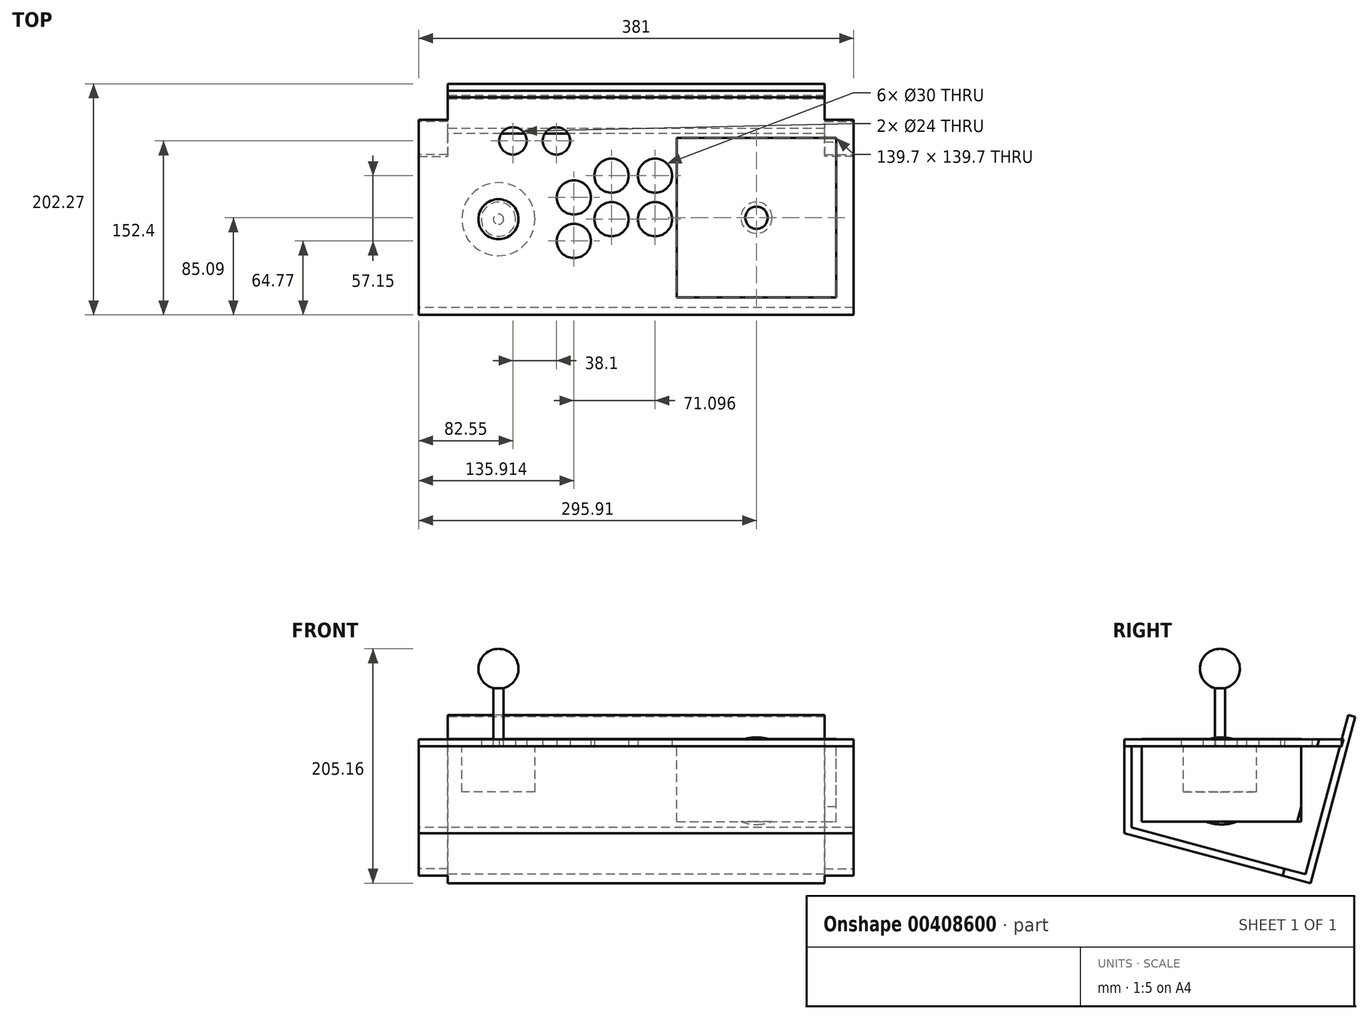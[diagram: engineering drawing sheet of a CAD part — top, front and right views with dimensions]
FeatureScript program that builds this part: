
annotation { "Feature Type Name" : "Feature", "Feature Type Description" : "" }
export const myFeature = defineFeature(function(context is Context, id is Id, definition is map)
    precondition{}
    {
        {
            assignVariable(context, id + "F0", {"variableType" : VariableType.LENGTH, "name" : "EndWidth", "lengthValue" : 381 * mm});
        }
        {
            assignVariable(context, id + "F1", {"variableType" : VariableType.LENGTH, "name" : "StickInset", "lengthValue" : 69.85 * mm});
        }
        {
            var Q0;
            Q0=qCreatedBy(makeId("Top.planeOp"),FACE);
            var sketch = newSketch(context, id + "F2", { "sketchPlane" : qUnion([Q0])});
            skLineSegment(sketch, "E0", {"start": v(0, 0) * mm, "end": v(381, 0) * mm});
            skLineSegment(sketch, "E1", {"start": v(381, 0) * mm, "end": v(381, 171.45) * mm});
            skLineSegment(sketch, "E2", {"start": v(381, 171.45) * mm, "end": v(361.95, 171.45) * mm});
            skLineSegment(sketch, "E3", {"start": v(361.95, 171.45) * mm, "end": v(361.95, 190.5) * mm});
            skLineSegment(sketch, "E4", {"start": v(0, 0) * mm, "end": v(0, 171.45) * mm});
            skLineSegment(sketch, "E5", {"start": v(0, 171.45) * mm, "end": v(19.05, 171.45) * mm});
            skLineSegment(sketch, "E6", {"start": v(19.05, 171.45) * mm, "end": v(19.05, 190.5) * mm});
            skCircle(sketch, "E7", {"center": v(82.55, 152.4) * mm, "radius": 12 * mm});
            skCircle(sketch, "E8", {"center": v(120.65, 152.4) * mm, "radius": 12 * mm});
            skCircle(sketch, "E9", {"center": v(135.91, 102.87) * mm, "radius": 15 * mm});
            skCircle(sketch, "E10", {"center": v(168.91, 121.92) * mm, "radius": 15 * mm});
            skCircle(sketch, "E11", {"center": v(207.01, 121.92) * mm, "radius": 15 * mm});
            skLineSegment(sketch, "E12", {"start": v(135.91, 102.87) * mm, "end": v(168.91, 121.92) * mm, "construction": true});
            skLineSegment(sketch, "E13", {"start": v(207.01, 121.92) * mm, "end": v(168.91, 121.92) * mm, "construction": true});
            skCircle(sketch, "E14", {"center": v(135.91, 64.77) * mm, "radius": 15 * mm});
            skCircle(sketch, "E15", {"center": v(168.91, 83.82) * mm, "radius": 15 * mm});
            skCircle(sketch, "E16", {"center": v(207.01, 83.82) * mm, "radius": 15 * mm});
            skLineSegment(sketch, "E17", {"start": v(135.91, 64.77) * mm, "end": v(168.91, 83.82) * mm, "construction": true});
            skLineSegment(sketch, "E18", {"start": v(207.01, 83.82) * mm, "end": v(168.91, 83.82) * mm, "construction": true});
            skLineSegment(sketch, "E19", {"start": v(168.91, 121.92) * mm, "end": v(168.91, 83.82) * mm, "construction": true});
            skLineSegment(sketch, "E20", {"start": v(82.55, 152.4) * mm, "end": v(120.65, 152.4) * mm, "construction": true});
            skPoint(sketch, "E21", {"position": v(168.91, 102.87) * mm});
            skLineSegment(sketch, "E22", {"start": v(135.91, 64.77) * mm, "end": v(135.91, 102.87) * mm, "construction": true});
            skCircle(sketch, "E23", {"center": v(69.85, 83.82) * mm, "radius": 15 * mm});
            skLineSegment(sketch, "E24.bottom", {"start": v(226.06, 154.94) * mm, "end": v(365.76, 154.94) * mm});
            skLineSegment(sketch, "E24.top", {"start": v(226.06, 15.24) * mm, "end": v(365.76, 15.24) * mm});
            skLineSegment(sketch, "E24.left", {"start": v(226.06, 154.94) * mm, "end": v(226.06, 15.24) * mm});
            skLineSegment(sketch, "E24.right", {"start": v(365.76, 154.94) * mm, "end": v(365.76, 15.24) * mm});
            skLineSegment(sketch, "E25", {"start": v(19.05, 190.5) * mm, "end": v(361.95, 190.5) * mm});
            skSolve(sketch);
        }
        {
            var Q0;
            Q0=makeQuery(id+"F2.imprint","IMPRINT",FACE,{"disambiguationData":[TD([[makeQuery(id+"F2.imprint","IMPRINT",EDGE,{"derivedFrom":sQuery(id+"F2.wireOp",EDGE,"E0")}),1.0]])]});
            extrude(context, id + "F3", {"entities" : qUnion([Q0]), "depth" : 6 * mm, "offsetDistance" : 25.4 * mm});
        }
        {
            var Q0;
            Q0=makeQuery(id+"F3.opExtrude","CAP_EDGE",EDGE,{"disambiguationData":[OSD([sQuery(id+"F2.wireOp",EDGE,"E24.bottom")])],"isStart":true});
            cPoint(context, id + "F4", {"entities" : qUnion([Q0]), "parameter" : 0.5});
        }
        {
            var Q0;
            Q0=makeQuery(id+"F3.opExtrude","CAP_EDGE",EDGE,{"disambiguationData":[OSD([sQuery(id+"F2.wireOp",EDGE,"E24.bottom")])],"isStart":false});
            cPoint(context, id + "F5", {"entities" : qUnion([Q0]), "parameter" : 0.5});
        }
        {
            var Q0;
            Q0=makeQuery(id+"F3.opExtrude","CAP_EDGE",EDGE,{"disambiguationData":[OSD([sQuery(id+"F2.wireOp",EDGE,"E24.top")])],"isStart":false});
            cPoint(context, id + "F6", {"entities" : qUnion([Q0]), "parameter" : 0.5});
        }
        {
            var Q0;
            Q0 = qCreatedBy(id + "F4" ,VERTEX);
            var Q1;
            Q1 = qCreatedBy(id + "F5" ,VERTEX);
            var Q2;
            Q2 = qCreatedBy(id + "F6" ,VERTEX);
            cPlane(context, id + "F7", {"entities" : qUnion([Q0, Q1, Q2]), "cplaneType" : CPlaneType.THREE_POINT, "offset" : 25.4 * mm, "width" : 152.4 * mm, "height" : 152.4 * mm});
        }
        {
            var Q0;
            Q0=qCreatedBy(makeId("Right.planeOp"),FACE);
            cPlane(context, id + "F8", {"entities" : qUnion([Q0]), "cplaneType" : CPlaneType.OFFSET, "offset" : getVariable(context, 'StickInset'), "width" : 152.4 * mm, "height" : 152.4 * mm});
        }
        {
            var Q0;
            Q0=qCreatedBy(id+"F8.planeOp",FACE);
            var sketch = newSketch(context, id + "F9", { "sketchPlane" : qUnion([Q0])});
            skArc(sketch, "E26", {"start": v(83.82, 85.21) * mm, "mid": v(66.47, 69.98) * mm, "end": v(79.32, 50.8) * mm});
            skLineSegment(sketch, "E27", {"start": v(83.82, 85.21) * mm, "end": v(83.82, -40) * mm});
            skLineSegment(sketch, "E28.0", {"start": v(79.32, 50.8) * mm, "end": v(79.32, 0) * mm});
            skLineSegment(sketch, "E29", {"start": v(83.82, -40) * mm, "end": v(51.82, -40) * mm});
            skLineSegment(sketch, "E30", {"start": v(51.82, -40) * mm, "end": v(51.82, 0) * mm});
            skLineSegment(sketch, "E31", {"start": v(51.82, 0) * mm, "end": v(79.32, 0) * mm});
            skPoint(sketch, "E32.orphan", {"position": v(83.82, 102.1) * mm});
            skSolve(sketch);
        }
        {
            var Q0;
            Q0 = qSketchRegion(id + "F9", true);
            var Q1;
            Q1=sQuery(id+"F9.wireOp",EDGE,"E27");
            revolve(context, id + "F10", {"operationType" : NewBodyOperationType.ADD, "surfaceOperationType" : NewSurfaceOperationType.NEW, "entities" : qUnion([Q0]), "axis" : qUnion([Q1]), "revolveType" : RevolveType.FULL});
        }
        {
            var Q0;
            Q0=qCreatedBy(id+"F7.planeOp",FACE);
            var sketch = newSketch(context, id + "F11", { "sketchPlane" : qUnion([Q0])});
            skArc(sketch, "E33", {"start": v(-85.1, -68.58) * mm, "mid": v(-47, -30.48) * mm, "end": v(-85.1, 7.62) * mm});
            skLineSegment(sketch, "E34", {"start": v(-85.1, 7.62) * mm, "end": v(-85.1, -68.58) * mm});
            skSolve(sketch);
        }
        {
            var Q0;
            Q0=makeQuery(id+"F11.imprint","IMPRINT",FACE,{"disambiguationData":[TD([[makeQuery(id+"F11.imprint","IMPRINT",EDGE,{"derivedFrom":sQuery(id+"F11.wireOp",EDGE,"E33")}),1.0]])]});
            var Q1;
            Q1=sQuery(id+"F11.wireOp",EDGE,"E34");
            revolve(context, id + "F12", {"operationType" : NewBodyOperationType.ADD, "surfaceOperationType" : NewSurfaceOperationType.NEW, "entities" : qUnion([Q0]), "axis" : qUnion([Q1]), "revolveType" : RevolveType.FULL, "oppositeDirection" : true});
        }
        {
            var Q0;
            Q0=makeQuery(id+"F2.imprint","IMPRINT",FACE,{"disambiguationData":[TD([[makeQuery(id+"F2.imprint","IMPRINT",EDGE,{"derivedFrom":sQuery(id+"F2.wireOp",EDGE,"E24.bottom")}),-1.0]])]});
            extrude(context, id + "F13", {"entities" : qUnion([Q0]), "operationType" : NewBodyOperationType.ADD, "oppositeDirection" : true, "depth" : 66.04 * mm, "offsetDistance" : 25.4 * mm, "hasSecondDirection" : true, "secondDirectionOppositeDirection" : true, "secondDirectionDepth" : -6.35 * mm});
        }
        {
            var Q0;
            Q0=qCreatedBy(makeId("Right.planeOp"),FACE);
            var sketch = newSketch(context, id + "F14", { "sketchPlane" : qUnion([Q0])});
            skLineSegment(sketch, "E35", {"start": v(0, 0) * mm, "end": v(0, -76.2) * mm});
            skLineSegment(sketch, "E36", {"start": v(0, -76.2) * mm, "end": v(163.29, -119.95) * mm});
            skLineSegment(sketch, "E37", {"start": v(6.35, 0) * mm, "end": v(6.35, -77.9) * mm});
            skLineSegment(sketch, "E38", {"start": v(196.14, 27.17) * mm, "end": v(190.57, 6.4) * mm});
            skLineSegment(sketch, "E39", {"start": v(0, 0) * mm, "end": v(6.35, 0) * mm});
            skLineSegment(sketch, "E40", {"start": v(6.35, -71.33) * mm, "end": v(158.8, -112.18) * mm});
            skLineSegment(sketch, "E41", {"start": v(158.8, -112.18) * mm, "end": v(164.93, -113.82) * mm});
            skLineSegment(sketch, "E42", {"start": v(164.93, -113.82) * mm, "end": v(163.29, -119.95) * mm});
            skLineSegment(sketch, "E43", {"start": v(164.93, -113.82) * mm, "end": v(202.27, 25.53) * mm});
            skLineSegment(sketch, "E44", {"start": v(202.27, 25.53) * mm, "end": v(196.14, 27.17) * mm});
            skLineSegment(sketch, "E45", {"start": v(190.57, 6.4) * mm, "end": v(192.1, 6) * mm});
            skLineSegment(sketch, "E46", {"start": v(192.1, 6) * mm, "end": v(190.39, -0.41) * mm});
            skLineSegment(sketch, "E47", {"start": v(190.39, -0.41) * mm, "end": v(188.86, 0) * mm});
            skLineSegment(sketch, "E48.trimOffspring", {"start": v(188.86, 0) * mm, "end": v(158.8, -112.18) * mm});
            skSolve(sketch);
        }
        {
            var Q0;
            Q0=makeQuery(id+"F14.imprint","IMPRINT",FACE,{"disambiguationData":[TD([[makeQuery(id+"F14.imprint","IMPRINT",EDGE,{"derivedFrom":sQuery(id+"F14.wireOp",EDGE,"E38")}),1.0]])]});
            var Q1;
            {var subQ0=sQuery(id+"F14.wireOp",EDGE,"E40");Q1=makeQuery(id+"F14.imprint","IMPRINT",FACE,{"disambiguationData":[TD([[makeQuery(id+"F14.imprint","IMPRINT",EDGE,{"derivedFrom":subQ0}),-1.0]])]});}
            var Q2;
            {var subQ5=sQuery(id+"F14.wireOp",EDGE,"E35");Q2=makeQuery(id+"F14.imprint","IMPRINT",FACE,{"disambiguationData":[TD([[makeQuery(id+"F14.imprint","IMPRINT",EDGE,{"derivedFrom":subQ5}),1.0]])]});}
            extrude(context, id + "F15", {"entities" : qUnion([Q0, Q1, Q2]), "depth" : getVariable(context, 'EndWidth'), "offsetDistance" : 25.4 * mm});
        }
        {
            var Q0;
            Q0=makeQuery(id+"F15.opExtrude","SWEPT_FACE",FACE,{"disambiguationData":[OSD([sQuery(id+"F14.wireOp",EDGE,"E36")])]});
            var sketch = newSketch(context, id + "F16", { "sketchPlane" : qUnion([Q0])});
            skLineSegment(sketch, "E49.bottom", {"start": v(381, -163.37) * mm, "end": v(355.6, -163.37) * mm});
            skLineSegment(sketch, "E49.top", {"start": v(381, -188.77) * mm, "end": v(355.6, -188.77) * mm});
            skLineSegment(sketch, "E49.left", {"start": v(381, -163.37) * mm, "end": v(381, -188.77) * mm});
            skLineSegment(sketch, "E49.right", {"start": v(355.6, -163.37) * mm, "end": v(355.6, -188.77) * mm});
            skPoint(sketch, "E50", {"position": v(190.5, -19.72) * mm});
            skPoint(sketch, "E51", {"position": v(190.5, -188.77) * mm});
            skLineSegment(sketch, "E52", {"start": v(190.5, -19.72) * mm, "end": v(190.5, -188.77) * mm, "construction": true});
            skLineSegment(sketch, "E53.MirrorCS", {"start": v(0, -163.37) * mm, "end": v(0, -188.77) * mm});
            skLineSegment(sketch, "E54.MirrorCS", {"start": v(0, -163.37) * mm, "end": v(25.4, -163.37) * mm});
            skLineSegment(sketch, "E55.MirrorCS", {"start": v(25.4, -163.37) * mm, "end": v(25.4, -188.77) * mm});
            skLineSegment(sketch, "E56.MirrorCS", {"start": v(0, -188.77) * mm, "end": v(25.4, -188.77) * mm});
            skSolve(sketch);
        }
        {
            var Q0;
            Q0=makeQuery(id+"F16.imprint","IMPRINT",FACE,{"disambiguationData":[TD([[makeQuery(id+"F16.imprint","IMPRINT",EDGE,{"derivedFrom":sQuery(id+"F16.wireOp",EDGE,"E49.bottom")}),1.0]])]});
            var Q1;
            Q1=makeQuery(id+"F16.imprint","IMPRINT",FACE,{"disambiguationData":[TD([[makeQuery(id+"F16.imprint","IMPRINT",EDGE,{"derivedFrom":sQuery(id+"F16.wireOp",EDGE,"E53.MirrorCS")}),1.0]])]});
            extrude(context, id + "F17", {"entities" : qUnion([Q0, Q1]), "operationType" : NewBodyOperationType.REMOVE, "oppositeDirection" : true, "depth" : 203.2 * mm, "offsetDistance" : 25.4 * mm});
        }
    });
